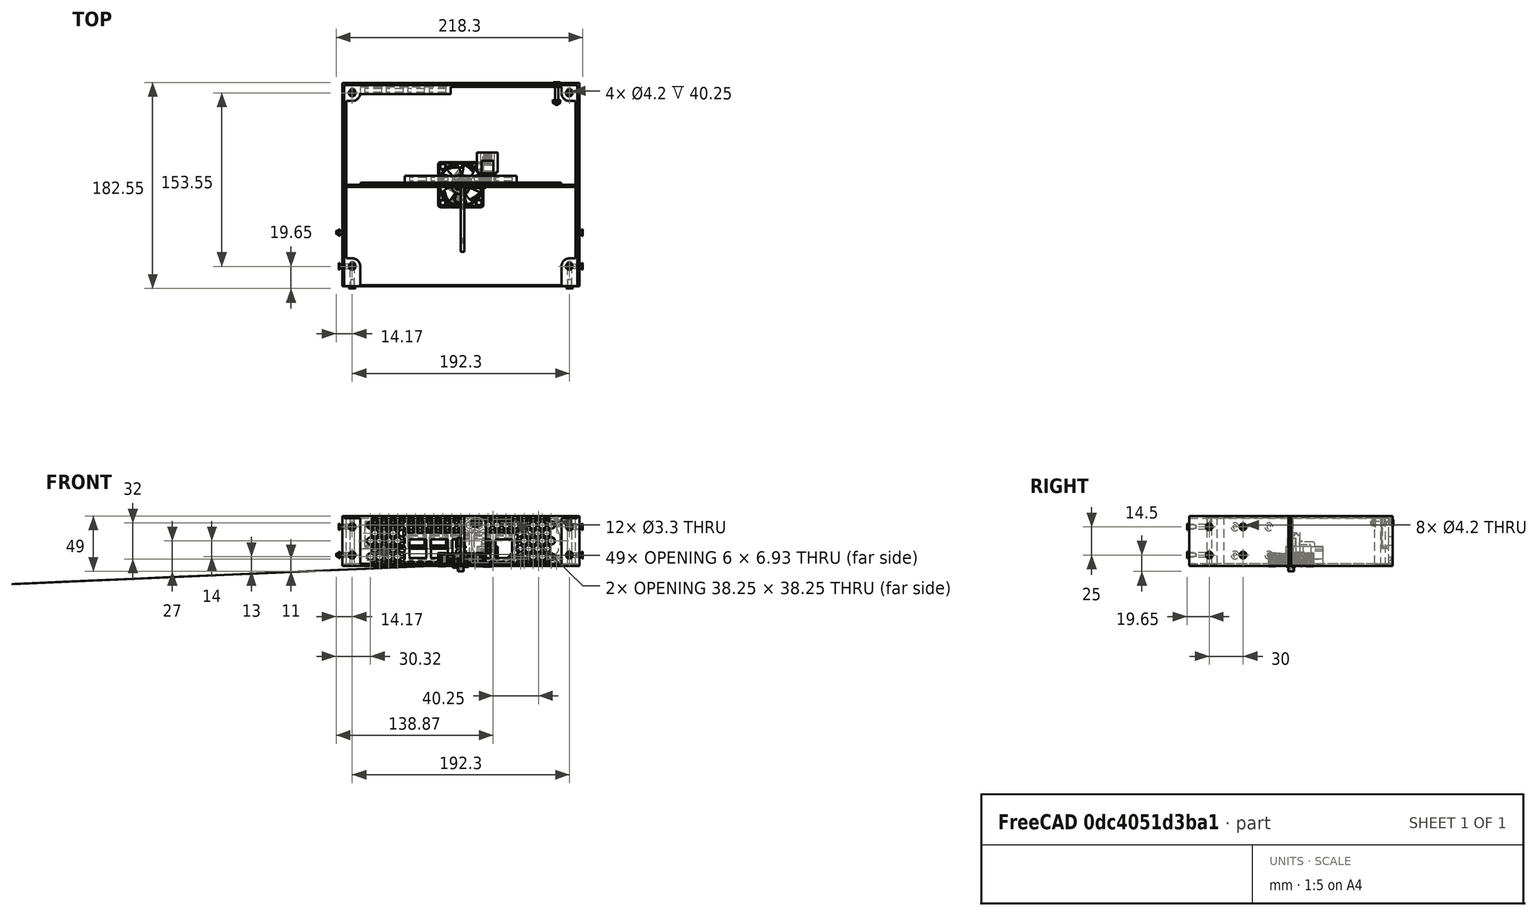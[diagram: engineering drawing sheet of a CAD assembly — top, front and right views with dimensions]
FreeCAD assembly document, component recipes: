
FREECAD ASSEMBLY — COMPONENT RECIPES ("Rack box")

This assembly document has 6 components, labeled P0..P5 below (a component is one placed body or linked part). 5 of them carry a construction recipe — the FreeCAD feature program that regenerates the part from scratch, quoted from this document or its linked companion documents; the rest are supplied as boundary geometry only. No exploded tour is included for this assembly.
COMPONENT P0 — recipe-attached ("Box001", modeled in this document).
Construction recipe (the document's own serialized feature program — sketch geometry with constraints, then the solid features built on it; lengths are millimeters unless a unit is written):

FEATURE [Sketcher::SketchObject] Sketch
  ArcFitTolerance = 1e-06
  AttachmentSupport = -> [XY_Plane002]
  ExternalTypes = [0]
  FullyConstrained = true
  MakeInternals = false
  MapMode = 2
  expr: Constraints[10] = <<Params>>.boxWidth
  expr: Constraints[11] = <<Params>>.boxLength
  sketch-geometry (5):
    g0: LineSegment StartX=-105 StartY=90 StartZ=0 EndX=-105 EndY=-90 EndZ=0
    g1: LineSegment StartX=-105 StartY=-90 StartZ=0 EndX=105 EndY=-90 EndZ=0
    g2: LineSegment StartX=105 StartY=-90 StartZ=0 EndX=105 EndY=90 EndZ=0
    g3: LineSegment StartX=105 StartY=90 StartZ=0 EndX=-105 EndY=90 EndZ=0
    g4: GeomPoint [constr] X=2e-16 Y=-2e-16 Z=0
  constraints (12):
    c: Coincident(g0,g1)
    c: Coincident(g1,g2)
    c: Coincident(g2,g3)
    c: Coincident(g3,g0)
    c: Vertical(g0)
    c: Vertical(g2)
    c: Horizontal(g1)
    c: Horizontal(g3)
    c: Symmetric(g2,g0,g4)
    c: Coincident(g4,g-1)
    c: DistanceX(g3,g3) = 210
    c: DistanceY(g2,g2) = 180
FEATURE [PartDesign::Pad] Pad  label="PROBLEMATIC_PAD"
  Direction = (0,0,1)
  Length = 44
  Length2 = 10
  Profile = -> Sketch
  ReferenceAxis = -> Sketch [N_Axis]
  Refine = true
  SideType = 0
  Suppressed = false
  Type = 0
  Type2 = 0
  expr: Length = <<Params>>.boxHeight * <<Params>>.rackUnit - <<Params>>.rackUnitTolerance
FEATURE [Sketcher::SketchObject] Sketch001
  ArcFitTolerance = 1e-06
  AttachmentSupport = -> [Pad]
  ExternalTypes = [0]
  FullyConstrained = true
  MakeInternals = false
  MapMode = 5
  Placement = pos=(0,0,44) rot=(0,0,1;0rad)
  expr: Constraints[10] = <<Params>>.boxWidth - 2 * <<Params>>.wallThickness
  expr: Constraints[11] = <<Params>>.boxLength - <<Params>>.wallThickness
  expr: Constraints[12] = <<Params>>.boxLength / 2 - <<Params>>.wallThickness
  sketch-geometry (5):
    g0: LineSegment StartX=-103.25 StartY=-90 StartZ=0 EndX=103.25 EndY=-90 EndZ=0
    g1: LineSegment StartX=103.25 StartY=-90 StartZ=0 EndX=103.25 EndY=88.25 EndZ=0
    g2: LineSegment StartX=103.25 StartY=88.25 StartZ=0 EndX=-103.25 EndY=88.25 EndZ=0
    g3: LineSegment StartX=-103.25 StartY=88.25 StartZ=0 EndX=-103.25 EndY=-90 EndZ=0
    g4: GeomPoint X=0 Y=-90 Z=0
  constraints (13):
    c: Coincident(g0,g1)
    c: Coincident(g1,g2)
    c: Coincident(g2,g3)
    c: Coincident(g3,g0)
    c: Horizontal(g0)
    c: Horizontal(g2)
    c: Vertical(g1)
    c: Vertical(g3)
    c: Symmetric(g0,g0,g4)
    c: PointOnObject(g4,g-2)
    c: DistanceX(g2,g2) = 206.5
    c: DistanceY(g3,g3) = 178.25
    c: DistanceY(g-1,g2) = 88.25
FEATURE [PartDesign::Pocket] Pocket
  BaseFeature = -> Pad
  Direction = (0,0,-1)
  Length = 0
  Length2 = 5
  Offset = -1.75
  Profile = -> Sketch001
  ReferenceAxis = -> Sketch001 [N_Axis]
  Refine = true
  SideType = 0
  Suppressed = false
  Type = 3
  Type2 = 0
  UpToFace = -> Pad [Face5]
  expr: Offset = -<<Params>>.wallThickness
FEATURE [Sketcher::SketchObject] Sketch002
  ArcFitTolerance = 1e-06
  AttachmentSupport = -> [Pocket]
  ExternalTypes = [0]
  FullyConstrained = true
  MakeInternals = false
  MapMode = 5
  Placement = pos=(0,0,1.75) rot=(0,0,1;0rad)
  expr: Constraints[0] = <<Params>>.M3InsertDiam
  expr: Constraints[23] = <<Params>>.boxWidth / 2 - <<Params>>.wallThickness
  expr: Constraints[25] = 17.6 mm
  expr: Constraints[26] = <<Params>>.boxLength / 2
  expr: Constraints[31] = <<Params>>.boxLength - <<Params>>.wallThickness
  expr: Constraints[36] = <<Params>>.wallThickness
  expr: Constraints[65] = <<Params>>.wallThickness
  sketch-geometry (27):
    g0: Circle CenterX=-96.15 CenterY=81.15 CenterZ=0 NormalX=0 NormalY=0 NormalZ=1 AngleXU=0 Radius=2.1
    g1: LineSegment StartX=-89.05 StartY=-90 StartZ=0 EndX=-89.05 EndY=-72.4 EndZ=0
    g2: Circle CenterX=-96.15 CenterY=-72.4 CenterZ=0 NormalX=0 NormalY=0 NormalZ=1 AngleXU=0 Radius=2.1
    g3: ArcOfCircle CenterX=-96.15 CenterY=81.15 CenterZ=0 NormalX=0 NormalY=0 NormalZ=1 AngleXU=0 Radius=7.1 StartAngle=4.71239 EndAngle=6.28319
    g4: ArcOfCircle CenterX=-96.15 CenterY=-72.4 CenterZ=0 NormalX=0 NormalY=0 NormalZ=1 AngleXU=0 Radius=7.1 StartAngle=2e-16 EndAngle=1.5708
    g5: LineSegment [constr] StartX=-96.15 StartY=81.15 StartZ=0 EndX=-96.15 EndY=-72.4 EndZ=0
    g6: LineSegment StartX=-89.05 StartY=-90 StartZ=0 EndX=-103.25 EndY=-90 EndZ=0
    g7: LineSegment StartX=-101.5 StartY=74.05 StartZ=0 EndX=-101.5 EndY=-65.3 EndZ=0
    g8: LineSegment StartX=-96.15 StartY=74.05 StartZ=0 EndX=-101.5 EndY=74.05 EndZ=0
    g9: LineSegment StartX=-101.5 StartY=-65.3 StartZ=0 EndX=-96.15 EndY=-65.3 EndZ=0
    g10: LineSegment StartX=-103.25 StartY=-90 StartZ=0 EndX=-103.25 EndY=88.25 EndZ=0
    g11: LineSegment StartX=-89.05 StartY=86.5 StartZ=0 EndX=0 EndY=86.5 EndZ=0
    g12: LineSegment StartX=-89.05 StartY=81.15 StartZ=0 EndX=-89.05 EndY=86.5 EndZ=0
    g13: LineSegment StartX=-103.25 StartY=88.25 StartZ=0 EndX=0 EndY=88.25 EndZ=0
    g14: LineSegment StartX=103.25 StartY=88.25 StartZ=0 EndX=0 EndY=88.25 EndZ=0
    g15: LineSegment StartX=89.05 StartY=86.5 StartZ=0 EndX=0 EndY=86.5 EndZ=0
    g16: LineSegment StartX=89.05 StartY=81.15 StartZ=0 EndX=89.05 EndY=86.5 EndZ=0
    g17: ArcOfCircle CenterX=96.15 CenterY=81.15 CenterZ=0 NormalX=0 NormalY=0 NormalZ=1 AngleXU=0 Radius=7.1 StartAngle=3.14159 EndAngle=4.71239
    g18: LineSegment StartX=96.15 StartY=74.05 StartZ=0 EndX=101.5 EndY=74.05 EndZ=0
    g19: LineSegment StartX=103.25 StartY=-90 StartZ=0 EndX=103.25 EndY=88.25 EndZ=0
    g20: Circle CenterX=96.15 CenterY=81.15 CenterZ=0 NormalX=0 NormalY=0 NormalZ=1 AngleXU=0 Radius=2.1
    g21: ArcOfCircle CenterX=96.15 CenterY=-72.4 CenterZ=0 NormalX=0 NormalY=0 NormalZ=1 AngleXU=0 Radius=7.1 StartAngle=1.5708 EndAngle=3.14159
    g22: LineSegment StartX=89.05 StartY=-90 StartZ=0 EndX=89.05 EndY=-72.4 EndZ=0
    g23: LineSegment StartX=89.05 StartY=-90 StartZ=0 EndX=103.25 EndY=-90 EndZ=0
    g24: LineSegment StartX=101.5 StartY=-65.3 StartZ=0 EndX=96.15 EndY=-65.3 EndZ=0
    g25: LineSegment StartX=101.5 StartY=74.05 StartZ=0 EndX=101.5 EndY=-65.3 EndZ=0
    g26: Circle CenterX=96.15 CenterY=-72.4 CenterZ=0 NormalX=0 NormalY=0 NormalZ=1 AngleXU=0 Radius=2.1
  constraints (66):
    c: Diameter(g0) = 4.2
    c: Vertical(g1)
    c: Equal(g0,g2)
    c: Coincident(g3,g0)
    c: Coincident(g4,g2)
    c: Tangent(g4,g1) = -1.5708
    c: Coincident(g5,g0)
    c: Coincident(g5,g2)
    c: Vertical(g5)
    c: Distance(g2,g1) = 5
    c: Coincident(g6,g1)
    c: Vertical(g7)
    c: Coincident(g8,g7)
    c: Horizontal(g8)
    c: Tangent(g8,g3) = 1.5708
    c: Coincident(g9,g7)
    c: Horizontal(g9)
    c: Tangent(g9,g4) = 1.5708
    c: Coincident(g10,g6)
    c: Distance(g0,g10) = 5
    c: Distance(g3,g0) = 5
    c: Horizontal(g11)
    c: Coincident(g12,g11)
    c: DistanceX(g6,g-1) = 103.25
    c: Vertical(g10)
    c: DistanceY(g6,g2) = 17.6
    c: DistanceY(g6,g-1) = 90
    c: Horizontal(g6)
    c: PointOnObject(g11,g-2)
    c: Tangent(g12,g3) = -1.5708
    c: Vertical(g12)
    c: DistanceY(g10,g10) = 178.25
    c: Equal(g8,g12)
    c: Coincident(g13,g10)
    c: PointOnObject(g13,g-2)
    c: Horizontal(g13)
    c: Distance(g11,g13) = 1.75
    c: Equal(g0,g20)
    c: Symmetric(g0,g20,g-2)
    c: Symmetric(g1,g22,g-2)
    c: Symmetric(g1,g22,g-2)
    c: Equal(g3,g17)
    c: Symmetric(g3,g17,g-2)
    c: Symmetric(g3,g17,g-2)
    c: Equal(g4,g21)
    c: Symmetric(g4,g21,g-2)
    c: Symmetric(g4,g21,g-2)
    c: Symmetric(g6,g23,g-2)
    c: Symmetric(g6,g23,g-2)
    c: Symmetric(g7,g25,g-2)
    c: Symmetric(g7,g25,g-2)
    c: Symmetric(g8,g18,g-2)
    c: Symmetric(g8,g18,g-2)
    c: Symmetric(g9,g24,g-2)
    c: Symmetric(g9,g24,g-2)
    c: Symmetric(g10,g19,g-2)
    c: Symmetric(g10,g19,g-2)
    c: Symmetric(g11,g15,g-2)
    c: Symmetric(g12,g16,g-2)
    c: Symmetric(g12,g16,g-2)
    c: Symmetric(g13,g14,g-2)
    c: Coincident(g15,g11)
    c: Coincident(g14,g13)
    c: Equal(g2,g26)
    c: Symmetric(g2,g26,g-2)
    c: DistanceX(g10,g7) = 1.75
FEATURE [PartDesign::Pad] Pad001
  BaseFeature = -> Pocket
  Direction = (0,0,1)
  Length = 10
  Length2 = 10
  Offset = 2
  Profile = -> Sketch002
  ReferenceAxis = -> Sketch002 [N_Axis]
  Refine = true
  SideType = 0
  Suppressed = false
  Type = 3
  Type2 = 0
  UpToFace = -> Pocket [Face5]
  expr: Offset = <<Params>>.wallThickness + <<Params>>.fitTol
FEATURE [Sketcher::SketchObject] Sketch003
  ArcFitTolerance = 1e-06
  AttachmentSupport = -> [Pad001]
  ExternalTypes = [0]
  FullyConstrained = true
  MakeInternals = false
  MapMode = 5
  Placement = pos=(0,-90,0) rot=(1,0,0;1.5708rad)
  expr: .Constraints.frontHole = <<Params>>.M3InsertDiam
  expr: Constraints[10] = <<Params>>.rackUnit * <<Params>>.boxHeight - <<Params>>.rackUnitTolerance
  expr: Constraints[11] = <<Params>>.boxWidth / 2 - (<<Params>>.wallThickness + 5 + <<Params>>.M3InsertDiam / 2)
  expr: Constraints[9] = <<Params>>.boxHeight * <<Params>>.rackUnit - <<Params>>.rackUnitTolerance - 2 * <<Params>>.frontHoleTopBottomSpace
  sketch-geometry (9):
    g0: LineSegment [constr] StartX=-96.15 StartY=44 StartZ=0 EndX=-96.15 EndY=0 EndZ=0
    g1: GeomPoint [constr] X=-96.15 Y=22 Z=0
    g2: Circle CenterX=-96.15 CenterY=34.5 CenterZ=0 NormalX=0 NormalY=0 NormalZ=1 AngleXU=0 Radius=2.1
    g3: Circle CenterX=-96.15 CenterY=9.5 CenterZ=0 NormalX=0 NormalY=0 NormalZ=1 AngleXU=0 Radius=2.1
    g4: Circle CenterX=96.15 CenterY=34.5 CenterZ=0 NormalX=0 NormalY=0 NormalZ=1 AngleXU=0 Radius=2.1
    g5: Circle CenterX=96.15 CenterY=9.5 CenterZ=0 NormalX=0 NormalY=0 NormalZ=1 AngleXU=0 Radius=2.1
    g6: LineSegment [constr] StartX=-96.15 StartY=0 StartZ=0 EndX=0 EndY=0 EndZ=0
    g7: LineSegment [constr] StartX=-96.15 StartY=34.5 StartZ=0 EndX=-96.15 EndY=9.5 EndZ=0
    g8: GeomPoint [constr] X=-96.15 Y=22 Z=0
  constraints (19):
    c: Vertical(g0)
    c: Symmetric(g0,g0,g1)
    c: PointOnObject(g2,g0)
    c: Diameter(g2) = 4.2  'frontHole'
    c: Equal(g3,g2)
    c: Equal(g2,g4)
    c: Symmetric(g2,g4,g-2)
    c: Equal(g3,g5)
    c: Symmetric(g3,g5,g-2)
    c: DistanceY(g3,g2) = 25
    c: DistanceY(g-1,g0) = 44
    c: DistanceX(g0,g-1) = 96.15
    c: Coincident(g6,g0)
    c: Coincident(g6,g-1)
    c: Horizontal(g6)
    c: Coincident(g7,g2)
    c: Coincident(g7,g3)
    c: Symmetric(g7,g7,g8)
    c: Coincident(g8,g1)
FEATURE [PartDesign::Pocket] Pocket001
  BaseFeature = -> Pad001
  Direction = (0,1,-2e-16)
  Length = 17.6
  Length2 = 5
  Offset = 2.1
  Profile = -> Sketch003
  ReferenceAxis = -> Sketch003 [N_Axis]
  Refine = true
  SideType = 0
  Suppressed = false
  Type = 0
  Type2 = 0
  UpToShape = -> [Pad001]
  expr: Length = 17.6
  expr: Offset = <<Params>>.M3InsertDiam / 2
FEATURE [Sketcher::SketchObject] Sketch010
  ArcFitTolerance = 1e-06
  AttachmentSupport = -> [Pocket001]
  ExternalTypes = [0]
  FullyConstrained = true
  MakeInternals = false
  MapMode = 5
  Placement = pos=(-105,0,0) rot=(0.57735,-0.57735,-0.57735;2.0944rad)
  expr: Constraints[15] = <<Params>>.M3InsertDiam
  expr: Constraints[17] = <<Params>>.rackUnit * <<Params>>.boxHeight - <<Params>>.rackUnitTolerance - 2 * <<Params>>.frontHoleTopBottomSpace
  expr: Constraints[20] = (<<Params>>.rackUnit * <<Params>>.boxHeight - <<Params>>.rackUnitTolerance) / 2
  expr: Constraints[21] = <<Params>>.boxLength / 2 - 17.6
  sketch-geometry (9):
    g0: LineSegment [constr] StartX=72.4 StartY=34.5 StartZ=0 EndX=42.4 EndY=34.5 EndZ=0
    g1: LineSegment [constr] StartX=42.4 StartY=34.5 StartZ=0 EndX=42.4 EndY=9.5 EndZ=0
    g2: LineSegment [constr] StartX=42.4 StartY=9.5 StartZ=0 EndX=72.4 EndY=9.5 EndZ=0
    g3: LineSegment [constr] StartX=72.4 StartY=9.5 StartZ=0 EndX=72.4 EndY=34.5 EndZ=0
    g4: Circle CenterX=42.4 CenterY=9.5 CenterZ=0 NormalX=0 NormalY=0 NormalZ=1 AngleXU=0 Radius=2.1
    g5: Circle CenterX=72.4 CenterY=9.5 CenterZ=0 NormalX=0 NormalY=0 NormalZ=1 AngleXU=0 Radius=2.1
    g6: Circle CenterX=42.4 CenterY=34.5 CenterZ=0 NormalX=0 NormalY=0 NormalZ=1 AngleXU=0 Radius=2.1
    g7: Circle CenterX=72.4 CenterY=34.5 CenterZ=0 NormalX=0 NormalY=0 NormalZ=1 AngleXU=0 Radius=2.1
    g8: GeomPoint [constr] X=72.4 Y=22 Z=0
  constraints (22):
    c: Coincident(g0,g1)
    c: Coincident(g1,g2)
    c: Coincident(g2,g3)
    c: Coincident(g3,g0)
    c: Horizontal(g0)
    c: Horizontal(g2)
    c: Vertical(g1)
    c: Vertical(g3)
    c: PointOnObject(g5,g2)
    c: DistanceX(g2,g2) = 30
    c: Coincident(g4,g1)
    c: Coincident(g6,g0)
    c: Equal(g7,g6)
    c: Equal(g6,g4)
    c: Equal(g4,g5)
    c: Diameter(g4) = 4.2
    c: Coincident(g0,g7)
    c: DistanceY(g1,g1) = 25
    c: PointOnObject(g5,g3)
    c: Symmetric(g3,g3,g8)
    c: DistanceY(g-1,g8) = 22
    c: DistanceX(g-1,g5) = 72.4
FEATURE [PartDesign::Pocket] Pocket004
  BaseFeature = -> Pocket001
  Direction = (1,0,0)
  Length = 0
  Length2 = 5
  Offset = 7.1
  Profile = -> Sketch010
  ReferenceAxis = -> Sketch010 [N_Axis]
  Refine = true
  SideType = 0
  Suppressed = false
  Type = 3
  Type2 = 0
  UpToFace = -> Pocket001 [Face3]
  expr: Offset = <<Params>>.M3InsertDiam / 2 + 5
FEATURE [PartDesign::Mirrored] Mirrored002
  BaseFeature = -> Pocket004
  MirrorPlane = -> YZ_Plane002
  Originals = -> [Pocket004]
  Refine = true
  Suppressed = false
  TransformMode = 0
FEATURE [Sketcher::SketchObject] Sketch014
  ArcFitTolerance = 1e-06
  AttachmentSupport = -> [Pocket001]
  ExternalTypes = [0]
  FullyConstrained = true
  MakeInternals = false
  MapMode = 5
  Placement = pos=(0,86.5,0) rot=(1,0,0;1.5708rad)
  expr: Constraints[19] = <<Params>>.M3ScrewHole
  expr: Constraints[20] = 39 / 2
  expr: Constraints[56] = (<<Params>>.rackUnit * <<Params>>.boxHeight - <<Params>>.rackUnitTolerance) / 2 - 32 / 2 - (min(<<Params>>.boxHeight; <<Params>>.fanAmountY) - 1) * (40 + <<Params>>.fitTol) / 2
  expr: Constraints[57] = <<Params>>.boxWidth / 2 - (<<Params>>.wallThickness + 5 + <<Params>>.M3InsertDiam + 5) - <<Params>>.fitTol
  sketch-geometry (22):
    g0: LineSegment [constr] StartX=52.8 StartY=6 StartZ=0 EndX=84.8 EndY=6 EndZ=0
    g1: LineSegment [constr] StartX=84.8 StartY=6 StartZ=0 EndX=84.8 EndY=38 EndZ=0
    g2: LineSegment [constr] StartX=84.8 StartY=38 StartZ=0 EndX=52.8 EndY=38 EndZ=0
    g3: LineSegment [constr] StartX=52.8 StartY=38 StartZ=0 EndX=52.8 EndY=6 EndZ=0
    g4: Circle CenterX=52.8 CenterY=38 CenterZ=0 NormalX=0 NormalY=0 NormalZ=1 AngleXU=0 Radius=1.65
    g5: Circle CenterX=84.8 CenterY=38 CenterZ=0 NormalX=0 NormalY=0 NormalZ=1 AngleXU=0 Radius=1.65
    g6: Circle CenterX=52.8 CenterY=6 CenterZ=0 NormalX=0 NormalY=0 NormalZ=1 AngleXU=0 Radius=1.65
    g7: Circle CenterX=84.8 CenterY=6 CenterZ=0 NormalX=0 NormalY=0 NormalZ=1 AngleXU=0 Radius=1.65
    g8: LineSegment [constr] StartX=84.8 StartY=6 StartZ=0 EndX=52.8 EndY=38 EndZ=0
    g9: ArcOfCircle CenterX=68.8 CenterY=22 CenterZ=0 NormalX=0 NormalY=0 NormalZ=1 AngleXU=0 Radius=19.5 StartAngle=0.196432 EndAngle=1.37436
    g10: ArcOfCircle CenterX=68.8 CenterY=22 CenterZ=0 NormalX=0 NormalY=0 NormalZ=1 AngleXU=0 Radius=19.5 StartAngle=1.76723 EndAngle=2.94516
    g11: ArcOfCircle CenterX=68.8 CenterY=22 CenterZ=0 NormalX=0 NormalY=0 NormalZ=1 AngleXU=0 Radius=19.5 StartAngle=3.33802 EndAngle=4.51596
    g12: ArcOfCircle CenterX=68.8 CenterY=22 CenterZ=0 NormalX=0 NormalY=0 NormalZ=1 AngleXU=0 Radius=19.5 StartAngle=4.90882 EndAngle=6.08675
    g13: LineSegment StartX=49.675 StartY=25.8058 StartZ=0 EndX=49.675 EndY=18.1942 EndZ=0
    g14: LineSegment StartX=64.9942 StartY=2.875 StartZ=0 EndX=72.6058 EndY=2.875 EndZ=0
    g15: LineSegment StartX=87.925 StartY=18.1942 StartZ=0 EndX=87.925 EndY=25.8058 EndZ=0
    g16: LineSegment StartX=72.6058 StartY=41.125 StartZ=0 EndX=64.9942 EndY=41.125 EndZ=0
    g17: LineSegment [constr] StartX=48.8 StartY=2 StartZ=0 EndX=88.8 EndY=2 EndZ=0
    g18: LineSegment [constr] StartX=88.8 StartY=2 StartZ=0 EndX=88.8 EndY=42 EndZ=0
    g19: LineSegment [constr] StartX=88.8 StartY=42 StartZ=0 EndX=48.8 EndY=42 EndZ=0
    g20: LineSegment [constr] StartX=48.8 StartY=42 StartZ=0 EndX=48.8 EndY=2 EndZ=0
    g21: GeomPoint [constr] X=68.8 Y=22 Z=0
  constraints (58):
    c: Coincident(g0,g1)
    c: Coincident(g1,g2)
    c: Coincident(g2,g3)
    c: Coincident(g3,g0)
    c: Horizontal(g0)
    c: Horizontal(g2)
    c: Vertical(g1)
    c: Vertical(g3)
    c: Equal(g2,g3)
    c: DistanceX(g2,g2) = 32
    c: Coincident(g4,g2)
    c: Coincident(g5,g1)
    c: Coincident(g6,g0)
    c: Coincident(g7,g0)
    c: Coincident(g8,g0)
    c: Coincident(g8,g2)
    c: Equal(g4,g5)
    c: Equal(g5,g7)
    c: Equal(g7,g6)
    c: Diameter(g4) = 3.3
    c: Radius(g9) = 19.5
    c: Symmetric(g8,g8,g9)
    c: Coincident(g10,g9)
    c: Coincident(g11,g9)
    c: Coincident(g12,g9)
    c: Equal(g12,g10)
    c: Equal(g10,g11)
    c: Equal(g11,g9)
    c: Coincident(g13,g10)
    c: Coincident(g13,g11)
    c: Coincident(g14,g11)
    c: Coincident(g14,g12)
    c: Coincident(g15,g12)
    c: Coincident(g15,g9)
    c: Coincident(g16,g9)
    c: Coincident(g16,g10)
    c: Equal(g16,g14)
    c: Equal(g14,g13)
    c: Equal(g13,g15)
    c: Horizontal(g16)
    c: Horizontal(g14)
    c: Vertical(g13)
    c: Vertical(g15)
    c: Coincident(g17,g18)
    c: Coincident(g18,g19)
    c: Coincident(g19,g20)
    c: Coincident(g20,g17)
    c: Horizontal(g17)
    c: Horizontal(g19)
    c: Vertical(g18)
    c: Vertical(g20)
    c: Symmetric(g19,g17,g21)
    c: Distance(g18,g20) = 40
    c: Distance(g17,g19) = 40
    c: Symmetric(g8,g8,g21)
    c: Distance(g19,g16) = 0.875
    c: DistanceY(g-1,g0) = 6
    c: DistanceX(g-1,g17) = 88.8
FEATURE [PartDesign::Pocket] Pocket006  label="fanHole"
  BaseFeature = -> Mirrored002
  Direction = (0,1,-2e-16)
  Length = 5
  Length2 = 5
  Profile = -> Sketch014
  ReferenceAxis = -> Sketch014 [N_Axis]
  Refine = true
  SideType = 0
  Suppressed = false
  Type = 1
  Type2 = 0
FEATURE [PartDesign::LinearPattern] LinearPattern003
  Direction = -> Sketch014 [H_Axis]
  Length = 40.25
  Length2 = 100
  Mode = 1
  Mode2 = 0
  Occurrences = 2
  Occurrences2 = 1
  Offset = 40.25
  Offset2 = 10
  Refine = true
  Reversed = true
  Reversed2 = false
  SpacingPattern = [0]
  SpacingPattern2 = [0]
  Spacings = [-1]
  Suppressed = false
  TransformMode = 0
  expr: Occurrences = min(3; <<Params>>.fanAmountX)
  expr: Offset = 40 + <<Params>>.fitTol
FEATURE [PartDesign::LinearPattern] LinearPattern004
  Direction = -> Sketch014 [V_Axis]
  Length = 40.25
  Length2 = 100
  Mode = 1
  Mode2 = 0
  Occurrences = 1
  Occurrences2 = 1
  Offset = 40.25
  Offset2 = 10
  Refine = true
  Reversed2 = false
  SpacingPattern = [0]
  SpacingPattern2 = [0]
  Spacings2 = [0]
  Suppressed = false
  TransformMode = 0
  expr: Occurrences = min(<<Params>>.boxHeight; <<Params>>.fanAmountY)
  expr: Offset = 40 + <<Params>>.fitTol
FEATURE [Sketcher::SketchObject] Sketch030  label="KeystoneSlab"
  ArcFitTolerance = 1e-06
  AttachmentSupport = -> [Mirrored002]
  ExternalTypes = [0]
  FullyConstrained = true
  MakeInternals = false
  MapMode = 5
  Placement = pos=(0,90,0) rot=(0,0.707107,0.707107;3.14159rad)
  expr: Constraints[10] = 4.2 + (<<Params>>.keystoneHoleWidth + 4.2) * <<Params>>.keystoneBackX
  expr: Constraints[11] = <<Params>>.rackUnit - <<Params>>.rackUnitTolerance - <<Params>>.wallThickness - <<Params>>.fitTol
  expr: Constraints[8] = <<Params>>.boxWidth / 2 - (<<Params>>.wallThickness + 5 + <<Params>>.M3InsertDiam + 5)
  expr: Constraints[9] = 3 + <<Params>>.keystoneCatchHeight + 4
  sketch-geometry (4):
    g0: LineSegment StartX=89.05 StartY=42 StartZ=0 EndX=8.85 EndY=42 EndZ=0
    g1: LineSegment StartX=8.85 StartY=42 StartZ=0 EndX=8.85 EndY=15.2 EndZ=0
    g2: LineSegment StartX=8.85 StartY=15.2 StartZ=0 EndX=89.05 EndY=15.2 EndZ=0
    g3: LineSegment StartX=89.05 StartY=15.2 StartZ=0 EndX=89.05 EndY=42 EndZ=0
  constraints (12):
    c: Coincident(g0,g1)
    c: Coincident(g1,g2)
    c: Coincident(g2,g3)
    c: Coincident(g3,g0)
    c: Horizontal(g0)
    c: Horizontal(g2)
    c: Vertical(g1)
    c: Vertical(g3)
    c: DistanceX(g-1,g2) = 89.05
    c: DistanceY(g3,g3) = 26.8
    c: DistanceX(g2,g2) = 80.2
    c: DistanceY(g-1,g0) = 42
FEATURE [Sketcher::SketchObject] Sketch032  label="KeystoneHoleSketch"
  ArcFitTolerance = 1e-06
  AttachmentSupport = -> [Pad]
  ExternalTypes = [0]
  FullyConstrained = true
  MakeInternals = false
  MapMode = 5
  Placement = pos=(0,90,0) rot=(0,0.707107,0.707107;3.14159rad)
  expr: Constraints[10] = <<Params>>.boxWidth / 2 - (<<Params>>.wallThickness + 5 + <<Params>>.M3InsertDiam + 5) - 4.2
  expr: Constraints[11] = <<Params>>.rackUnit - <<Params>>.rackUnitTolerance - <<Params>>.wallThickness - <<Params>>.keystoneCatchHeight - 4.2 - <<Params>>.fitTol
  expr: Constraints[8] = <<Params>>.keystoneHoleWidth
  expr: Constraints[9] = <<Params>>.keystoneHoleHeight
  sketch-geometry (4):
    g0: LineSegment StartX=70.05 StartY=34.8 StartZ=0 EndX=70.05 EndY=18 EndZ=0
    g1: LineSegment StartX=70.05 StartY=18 StartZ=0 EndX=84.85 EndY=18 EndZ=0
    g2: LineSegment StartX=84.85 StartY=18 StartZ=0 EndX=84.85 EndY=34.8 EndZ=0
    g3: LineSegment StartX=84.85 StartY=34.8 StartZ=0 EndX=70.05 EndY=34.8 EndZ=0
  constraints (12):
    c: Coincident(g0,g1)
    c: Coincident(g1,g2)
    c: Coincident(g2,g3)
    c: Coincident(g3,g0)
    c: Vertical(g0)
    c: Vertical(g2)
    c: Horizontal(g1)
    c: Horizontal(g3)
    c: DistanceX(g3,g3) = 14.8
    c: DistanceY(g2,g2) = 16.8
    c: DistanceX(g-1,g1) = 84.85
    c: DistanceY(g-1,g1) = 18
FEATURE [Sketcher::SketchObject] Sketch034  label="CatchHolesSketchBack"
  ArcFitTolerance = 1e-06
  AttachmentSupport = -> [Mirrored002]
  ExternalTypes = [0]
  FullyConstrained = true
  MakeInternals = false
  MapMode = 5
  Placement = pos=(-89.05,0,0) rot=(0.57735,0.57735,0.57735;2.0944rad)
  expr: Constraints[21] = <<Params>>.keystoneCatchHeight
  expr: Constraints[22] = <<Params>>.rackUnit - <<Params>>.rackUnitTolerance - <<Params>>.wallThickness - <<Params>>.keystoneCatchHeight - 4.2 - <<Params>>.fitTol
  expr: Constraints[23] = <<Params>>.boxLength / 2 - <<Params>>.keystoneCatchDepth
  sketch-geometry (8):
    g0: LineSegment StartX=81.8 StartY=18 StartZ=0 EndX=81.8 EndY=16.5 EndZ=0
    g1: LineSegment StartX=81.8 StartY=16.5 StartZ=0 EndX=84.8 EndY=16.5 EndZ=0
    g2: LineSegment StartX=84.8 StartY=16.5 StartZ=0 EndX=84.8 EndY=18 EndZ=0
    g3: LineSegment StartX=84.8 StartY=18 StartZ=0 EndX=81.8 EndY=18 EndZ=0
    g4: LineSegment StartX=87.8 StartY=39.3 StartZ=0 EndX=87.8 EndY=37.8 EndZ=0
    g5: LineSegment StartX=87.8 StartY=37.8 StartZ=0 EndX=84.8 EndY=37.8 EndZ=0
    g6: LineSegment StartX=84.8 StartY=37.8 StartZ=0 EndX=84.8 EndY=39.3 EndZ=0
    g7: LineSegment StartX=84.8 StartY=39.3 StartZ=0 EndX=87.8 EndY=39.3 EndZ=0
  constraints (24):
    c: Coincident(g0,g1)
    c: Coincident(g1,g2)
    c: Coincident(g2,g3)
    c: Coincident(g3,g0)
    c: Vertical(g0)
    c: Vertical(g2)
    c: Horizontal(g1)
    c: Horizontal(g3)
    c: DistanceX(g3,g3) = 3
    c: DistanceY(g2,g2) = 1.5
    c: Coincident(g4,g5)
    c: Coincident(g5,g6)
    c: Coincident(g6,g7)
    c: Coincident(g7,g4)
    c: Vertical(g4)
    c: Vertical(g6)
    c: Horizontal(g5)
    c: Horizontal(g7)
    c: Equal(g5,g3)
    c: Equal(g6,g2)
    c: PointOnObject(g2,g6)
    c: DistanceY(g2,g5) = 19.8
    c: DistanceY(g-1,g2) = 18
    c: DistanceX(g-1,g0) = 81.8
FEATURE [PartDesign::LinearPattern] LinearPattern
  Direction = -> Sketch032 [H_Axis]
  Length = 57
  Length2 = 100
  Mode = 1
  Mode2 = 0
  Occurrences = 4
  Occurrences2 = 1
  Offset = 19
  Offset2 = 10
  Refine = true
  Reversed = true
  Reversed2 = false
  SpacingPattern = [0]
  SpacingPattern2 = [0]
  Spacings = [-1,-1,-1]
  Suppressed = false
  TransformMode = 0
  expr: Occurrences = <<Params>>.keystoneBackX
  expr: Offset = <<Params>>.keystoneHoleWidth + 4.2
FEATURE [PartDesign::Chamfer] Chamfer007
  Angle = 45
  Base = -> Pocket006 [Edge132,Edge152,Edge154,Edge134]
  BaseFeature = -> Pocket006
  ChamferType = 0
  FlipDirection = false
  Refine = true
  Size = 1.4
  Size2 = 1
  SupportTransform = false
  Suppressed = false
  UseAllEdges = false
FEATURE [PartDesign::MultiTransform] MultiTransform001
  BaseFeature = -> Chamfer007
  Originals = -> [Pocket006,Chamfer007]
  Refine = true
  Suppressed = false
  TransformMode = 0
  Transformations = -> [LinearPattern003,LinearPattern004]
FEATURE [PartDesign::Pad] Pad012  label="KeystoneSlabPad"
  BaseFeature = -> MultiTransform001
  Direction = (0,1,-2e-16)
  Length = 9.75
  Length2 = 10
  Profile = -> Sketch030
  ReferenceAxis = -> Sketch030 [N_Axis]
  Refine = true
  Reversed = true
  SideType = 0
  Suppressed = false
  Type = 0
  Type2 = 0
  expr: Length = <<Params>>.keystoneStopDepth
FEATURE [PartDesign::Pocket] Pocket011  label="KeystoneHolePocket001"
  BaseFeature = -> Pad012
  Direction = (0,-1,2e-16)
  Length = 5
  Length2 = 5
  Profile = -> Sketch032
  ReferenceAxis = -> Sketch032 [N_Axis]
  Refine = true
  SideType = 0
  Suppressed = false
  Type = 1
  Type2 = 0
FEATURE [Sketcher::SketchObject] Sketch033  label="KeystoneCatchSketch"
  ArcFitTolerance = 1e-06
  AttachmentSupport = -> [Pocket011]
  ExternalTypes = [0]
  FullyConstrained = true
  MakeInternals = false
  MapMode = 5
  Placement = pos=(0,80.25,-4.25e-14) rot=(1,0,0;1.5708rad)
  expr: Constraints[10] = <<Params>>.boxWidth / 2 - (<<Params>>.wallThickness + 5 + <<Params>>.M3InsertDiam + 5) - 4.2
  expr: Constraints[11] = <<Params>>.rackUnit - <<Params>>.rackUnitTolerance - <<Params>>.wallThickness - <<Params>>.keystoneCatchHeight - 4.2 - <<Params>>.fitTol
  expr: Constraints[8] = <<Params>>.keystoneCatchHeight
  expr: Constraints[9] = <<Params>>.keystoneHoleWidth
  sketch-geometry (4):
    g0: LineSegment StartX=-84.85 StartY=37.8 StartZ=0 EndX=-84.85 EndY=18 EndZ=0
    g1: LineSegment StartX=-84.85 StartY=18 StartZ=0 EndX=-70.05 EndY=18 EndZ=0
    g2: LineSegment StartX=-70.05 StartY=18 StartZ=0 EndX=-70.05 EndY=37.8 EndZ=0
    g3: LineSegment StartX=-70.05 StartY=37.8 StartZ=0 EndX=-84.85 EndY=37.8 EndZ=0
  constraints (12):
    c: Coincident(g0,g1)
    c: Coincident(g1,g2)
    c: Coincident(g2,g3)
    c: Coincident(g3,g0)
    c: Vertical(g0)
    c: Vertical(g2)
    c: Horizontal(g1)
    c: Horizontal(g3)
    c: DistanceY(g2,g2) = 19.8
    c: DistanceX(g3,g3) = 14.8
    c: DistanceX(g0,g-1) = 84.85
    c: DistanceY(g-1,g0) = 18
FEATURE [PartDesign::Pocket] Pocket012  label="KeystoneCatchPocket"
  BaseFeature = -> Pocket011
  Direction = (0,1,-2e-16)
  Length = 8.2
  Length2 = 5
  Profile = -> Sketch033
  ReferenceAxis = -> Sketch033 [N_Axis]
  Refine = true
  SideType = 0
  Suppressed = false
  Type = 0
  Type2 = 0
  expr: Length = <<Params>>.keystoneCatchDepth
FEATURE [PartDesign::Pocket] Pocket013  label="CatchHolesPocketBox"
  BaseFeature = -> Pocket012
  Direction = (-1,0,0)
  Length = 19
  Length2 = -4.2
  Profile = -> Sketch034
  ReferenceAxis = -> Sketch034 [N_Axis]
  Refine = true
  Reversed = true
  SideType = 1
  Suppressed = false
  Type = 0
  Type2 = 0
  expr: Length = <<Params>>.keystoneHoleWidth + 4.2
FEATURE [PartDesign::Chamfer] Chamfer006
  Angle = 45
  Base = -> Pocket013 [Edge99,Edge260,Edge97]
  BaseFeature = -> Pocket013
  ChamferType = 0
  FlipDirection = false
  Refine = true
  Size = 1
  Size2 = 1
  SupportTransform = false
  Suppressed = false
  UseAllEdges = false
FEATURE [PartDesign::MultiTransform] MultiTransform
  BaseFeature = -> Chamfer006
  Originals = -> [Pocket011,Pocket012,Pocket013,Chamfer006]
  Refine = true
  Suppressed = false
  TransformMode = 0
  Transformations = -> [LinearPattern]
FEATURE [PartDesign::Body] Body  label="box"
  AllowCompound = false
  Group = -> [Sketch,Pad,Sketch001,Pocket,Sketch002,Pad001,Sketch003,Pocket001,Sketch010,Pocket004,Mirrored002,Sketch014,Pocket006,Chamfer007,MultiTransform001,LinearPattern003,LinearPattern004,Sketch030,Pad012,Sketch032,Pocket011,Sketch033,Pocket012,Sketch034,Pocket013,Chamfer006,MultiTransform,LinearPattern]
  Origin = -> Origin002
  Tip = -> MultiTransform
COMPONENT P1 — recipe-attached ("Ear 3D001", modeled in this document).
Construction recipe (the document's own serialized feature program — sketch geometry with constraints, then the solid features built on it; lengths are millimeters unless a unit is written):

FEATURE [Sketcher::SketchObject] Sketch011
  ArcFitTolerance = 1e-06
  AttachmentSupport = -> [YZ_Plane013]
  ExternalTypes = [0]
  FullyConstrained = true
  MakeInternals = false
  MapMode = 5
  Placement = pos=(0,0,0) rot=(0.57735,0.57735,0.57735;2.0944rad)
  expr: Constraints[14] = <<Params>>.M3ScrewHole
  expr: Constraints[28] = <<Params>>.boxHeight * <<Params>>.rackUnit - <<Params>>.rackUnitTolerance - 2 * <<Params>>.frontHoleTopBottomSpace
  expr: Constraints[30] = <<Params>>.frontThickness + 17.6
  expr: Constraints[32] = (<<Params>>.rackUnit * <<Params>>.boxHeight - <<Params>>.rackUnitTolerance) / 2
  expr: Constraints[33] = <<Params>>.rackUnit * <<Params>>.boxHeight - <<Params>>.rackUnitTolerance
  sketch-geometry (14):
    g0: LineSegment StartX=0 StartY=44 StartZ=0 EndX=-59.6 EndY=44 EndZ=0
    g1: LineSegment StartX=-59.6 StartY=44 StartZ=0 EndX=-59.6 EndY=0 EndZ=0
    g2: LineSegment StartX=-59.6 StartY=0 StartZ=0 EndX=0 EndY=0 EndZ=0
    g3: LineSegment StartX=0 StartY=0 StartZ=0 EndX=0 EndY=44 EndZ=0
    g4: LineSegment [constr] StartX=-49.6 StartY=9.5 StartZ=0 EndX=-49.6 EndY=0 EndZ=0
    g5: Circle CenterX=-49.6 CenterY=34.5 CenterZ=0 NormalX=0 NormalY=0 NormalZ=1 AngleXU=0 Radius=1.65
    g6: Circle CenterX=-19.6 CenterY=34.5 CenterZ=0 NormalX=0 NormalY=0 NormalZ=1 AngleXU=0 Radius=1.65
    g7: Circle CenterX=-49.6 CenterY=9.5 CenterZ=0 NormalX=0 NormalY=0 NormalZ=1 AngleXU=0 Radius=1.65
    g8: Circle CenterX=-19.6 CenterY=9.5 CenterZ=0 NormalX=0 NormalY=0 NormalZ=1 AngleXU=0 Radius=1.65
    g9: LineSegment [constr] StartX=-49.6 StartY=34.5 StartZ=0 EndX=-19.6 EndY=34.5 EndZ=0
    g10: LineSegment [constr] StartX=-19.6 StartY=34.5 StartZ=0 EndX=-19.6 EndY=9.5 EndZ=0
    g11: LineSegment [constr] StartX=-19.6 StartY=9.5 StartZ=0 EndX=-49.6 EndY=9.5 EndZ=0
    g12: LineSegment [constr] StartX=-49.6 StartY=9.5 StartZ=0 EndX=-49.6 EndY=34.5 EndZ=0
    g13: GeomPoint [constr] X=-19.6 Y=22 Z=0
  constraints (36):
    c: Coincident(g0,g1)
    c: Coincident(g1,g2)
    c: Coincident(g2,g3)
    c: Coincident(g3,g0)
    c: Horizontal(g0)
    c: Horizontal(g2)
    c: Vertical(g1)
    c: Vertical(g3)
    c: PointOnObject(g4,g2)
    c: Vertical(g4)
    c: Coincident(g7,g4)
    c: Equal(g7,g5)
    c: Equal(g5,g6)
    c: Equal(g6,g8)
    c: Diameter(g7) = 3.3
    c: Coincident(g9,g5)
    c: Coincident(g9,g6)
    c: Horizontal(g9)
    c: Coincident(g10,g6)
    c: Coincident(g10,g8)
    c: Vertical(g10)
    c: Coincident(g11,g8)
    c: Coincident(g11,g4)
    c: Horizontal(g11)
    c: Coincident(g12,g4)
    c: Coincident(g12,g5)
    c: Vertical(g12)
    c: DistanceX(g9,g9) = 30
    c: DistanceY(g10,g10) = 25
    c: PointOnObject(g-1,g2)
    c: DistanceX(g8,g2) = 19.6
    c: Symmetric(g10,g10,g13)
    c: DistanceY(g-1,g13) = 22
    c: DistanceY(g3,g3) = 44
    c: PointOnObject(g-1,g3)
    c: DistanceX(g1,g8) = 40
FEATURE [PartDesign::Pad] Pad006
  Direction = (1,0,0)
  Length = 3
  Length2 = 10
  Placement = pos=(0,0,0) rot=(1,1,1;2.0944rad)
  Profile = -> Sketch011
  ReferenceAxis = -> Sketch011 [N_Axis]
  Refine = true
  SideType = 0
  Suppressed = false
  Type = 0
  Type2 = 0
  expr: Length = <<Params>>.rackEarThick3D
FEATURE [PartDesign::Chamfer] Chamfer003
  Angle = 45
  Base = -> Pad006 [Edge15,Edge18,Edge21,Edge24]
  BaseFeature = -> Pad006
  ChamferType = 0
  FlipDirection = false
  Placement = pos=(0,0,0) rot=(1,1,1;2.0944rad)
  Refine = true
  Size = 1.85
  Size2 = 1
  SupportTransform = false
  Suppressed = false
  UseAllEdges = false
  expr: Size = min(<<Params>>.iso10642coneDetph; <<Params>>.rackEarThick3D - 0.01)
FEATURE [Sketcher::SketchObject] Sketch012
  ArcFitTolerance = 1e-06
  AttachmentSupport = -> [Chamfer003]
  ExternalGeometry = -> [Chamfer003]
  ExternalTypes = [0]
  FullyConstrained = true
  MakeInternals = false
  MapMode = 5
  Placement = pos=(3,-7e-16,3e-16) rot=(0.57735,0.57735,0.57735;2.0944rad)
  expr: Constraints[10] = <<Params>>.rackEarThick3D
  sketch-geometry (4):
    g0: LineSegment StartX=3.6e-15 StartY=44 StartZ=0 EndX=-3 EndY=44 EndZ=0
    g1: LineSegment StartX=-3 StartY=44 StartZ=0 EndX=-3 EndY=0 EndZ=0
    g2: LineSegment StartX=-3 StartY=0 StartZ=0 EndX=3.6e-15 EndY=0 EndZ=0
    g3: LineSegment StartX=3.6e-15 StartY=0 StartZ=0 EndX=3.6e-15 EndY=44 EndZ=0
  constraints (11):
    c: Coincident(g0,g1)
    c: Coincident(g1,g2)
    c: Coincident(g2,g3)
    c: Coincident(g3,g0)
    c: Horizontal(g0)
    c: Horizontal(g2)
    c: Vertical(g1)
    c: Vertical(g3)
    c: Coincident(g0,g-3)
    c: PointOnObject(g-3,g2)
    c: DistanceX(g0,g0) = 3
FEATURE [PartDesign::Pad] Pad007
  BaseFeature = -> Chamfer003
  Direction = (1,0,0)
  Length = 19
  Length2 = 10
  Placement = pos=(0,0,0) rot=(1,1,1;2.0944rad)
  Profile = -> Sketch012
  ReferenceAxis = -> Sketch012 [N_Axis]
  Refine = true
  SideType = 0
  Suppressed = false
  Type = 0
  Type2 = 0
  expr: Length = (<<Params>>.rackTotalWidth - <<Params>>.boxWidth) / 2 - <<Params>>.rackEarThick3D
FEATURE [Sketcher::SketchObject] Sketch013
  ArcFitTolerance = 1e-06
  AttachmentSupport = -> [Pad007]
  ExternalTypes = [0]
  FullyConstrained = true
  MakeInternals = false
  MapMode = 5
  Placement = pos=(0,3e-16,0) rot=(0.57735,0.57735,0.57735;4.18879rad)
  expr: Constraints[0] = <<Params>>.rackHoleDiam
  expr: Constraints[18] = <<Params>>.rackHoleDiam / 2 + <<Params>>.fitTol
  expr: Constraints[1] = <<Params>>.boxHeight > 1 ? <<Params>>.rackUnit * <<Params>>.boxHeight - (<<Params>>.rackUnit - <<Params>>.rackUnitTolerance) : <<Params>>.rackHoleSpacing * 2
  expr: Constraints[6] = <<Params>>.boxHeight > 1 ? <<Params>>.rackUnit / 2 - <<Params>>.rackUnitTolerance / 2 : <<Params>>.rackUnit / 2 - <<Params>>.rackUnitTolerance / 2 - <<Params>>.rackHoleSpacing
  expr: Constraints[7] = (<<Params>>.rackHoleSpread - <<Params>>.boxWidth) / 2
  sketch-geometry (13):
    g0: Circle [constr] CenterX=37.875 CenterY=13.2625 CenterZ=0 NormalX=0 NormalY=0 NormalZ=1 AngleXU=0 Radius=3
    g1: LineSegment [constr] StartX=37.875 StartY=13.2625 StartZ=0 EndX=6.125 EndY=13.2625 EndZ=0
    g2: Circle [constr] CenterX=6.125 CenterY=13.2625 CenterZ=0 NormalX=0 NormalY=0 NormalZ=1 AngleXU=0 Radius=3
    g3: ArcOfCircle CenterX=6.125 CenterY=14.7625 CenterZ=0 NormalX=0 NormalY=0 NormalZ=1 AngleXU=0 Radius=3.25 StartAngle=2e-16 EndAngle=3.14159
    g4: ArcOfCircle CenterX=6.125 CenterY=11.7625 CenterZ=0 NormalX=0 NormalY=0 NormalZ=1 AngleXU=0 Radius=3.25 StartAngle=3.14159 EndAngle=6.28319
    g5: LineSegment StartX=9.375 StartY=14.7625 StartZ=0 EndX=9.375 EndY=11.7625 EndZ=0
    g6: LineSegment StartX=2.875 StartY=14.7625 StartZ=0 EndX=2.875 EndY=11.7625 EndZ=0
    g7: LineSegment [constr] StartX=6.125 StartY=14.7625 StartZ=0 EndX=6.125 EndY=11.7625 EndZ=0
    g8: ArcOfCircle CenterX=37.875 CenterY=14.7625 CenterZ=0 NormalX=0 NormalY=0 NormalZ=1 AngleXU=0 Radius=3.25 StartAngle=2e-16 EndAngle=3.14159
    g9: ArcOfCircle CenterX=37.875 CenterY=11.7625 CenterZ=0 NormalX=0 NormalY=0 NormalZ=1 AngleXU=0 Radius=3.25 StartAngle=3.14159 EndAngle=6.28319
    g10: LineSegment StartX=41.125 StartY=14.7625 StartZ=0 EndX=41.125 EndY=11.7625 EndZ=0
    g11: LineSegment StartX=34.625 StartY=14.7625 StartZ=0 EndX=34.625 EndY=11.7625 EndZ=0
    g12: LineSegment [constr] StartX=37.875 StartY=14.7625 StartZ=0 EndX=37.875 EndY=11.7625 EndZ=0
  constraints (30):
    c: Diameter(g0) = 6
    c: Distance(g1,g1) = 31.75
    c: Coincident(g2,g1)
    c: Equal(g2,g0)
    c: Coincident(g1,g0)
    c: Horizontal(g1)
    c: DistanceX(g-1,g1) = 6.125
    c: Distance(g1,g-1) = 13.2625
    c: Tangent(g3,g5) = 1.5708
    c: Tangent(g3,g6) = -1.5708
    c: Tangent(g4,g5) = 1.5708
    c: Tangent(g4,g6) = -1.5708
    c: Equal(g3,g4)
    c: Coincident(g7,g3)
    c: Coincident(g7,g4)
    c: Symmetric(g7,g7,g1)
    c: Vertical(g7)
    c: DistanceY(g4,g3) = 3
    c: Radius(g3) = 3.25
    c: Tangent(g8,g10) = 1.5708
    c: Tangent(g8,g11) = -1.5708
    c: Tangent(g9,g10) = 1.5708
    c: Tangent(g9,g11) = -1.5708
    c: Equal(g8,g9)
    c: Coincident(g12,g8)
    c: Coincident(g12,g9)
    c: Symmetric(g12,g12,g0)
    c: Vertical(g12)
    c: Equal(g8,g3)
    c: Equal(g5,g11)
FEATURE [PartDesign::Pocket] Pocket005
  BaseFeature = -> Pad007
  Direction = (0,-1,0)
  Length = 5
  Length2 = 5
  Placement = pos=(0,0,0) rot=(1,1,1;2.0944rad)
  Profile = -> Sketch013
  ReferenceAxis = -> Sketch013 [N_Axis]
  Refine = true
  SideType = 0
  Suppressed = false
  Type = 1
  Type2 = 0
FEATURE [PartDesign::Fillet] Fillet
  Base = -> Pocket005 [Edge13]
  BaseFeature = -> Pocket005
  Placement = pos=(0,0,0) rot=(1,1,1;2.0944rad)
  Radius = 1.5
  Refine = true
  SupportTransform = false
  Suppressed = false
  UseAllEdges = false
FEATURE [PartDesign::Fillet] Fillet001
  Base = -> Fillet [Edge21,Edge11]
  BaseFeature = -> Fillet
  Placement = pos=(0,0,0) rot=(1,1,1;2.0944rad)
  Radius = 6.2
  Refine = true
  SupportTransform = false
  Suppressed = false
  UseAllEdges = false
FEATURE [PartDesign::Body] Body004  label="3DEar"
  AllowCompound = false
  Group = -> [Sketch011,Pad006,Chamfer003,Sketch012,Pad007,Sketch013,Pocket005,Fillet,Fillet001]
  Origin = -> Origin011
  Tip = -> Fillet001
COMPONENT P2 — same part as P1; its construction recipe is shown at P1.
COMPONENT P3 — recipe-attached ("Front cover001", modeled in this document).
Construction recipe (the document's own serialized feature program — sketch geometry with constraints, then the solid features built on it; lengths are millimeters unless a unit is written):

FEATURE [Sketcher::SketchObject] Sketch016  label="CoverPlateSketch"
  ArcFitTolerance = 1e-06
  AttachmentSupport = -> [XZ_Plane018]
  ExternalTypes = [0]
  FullyConstrained = true
  MakeInternals = false
  MapMode = 5
  Placement = pos=(0,0,0) rot=(1,0,0;1.5708rad)
  expr: Constraints[11] = <<Params>>.boxHeight * <<Params>>.rackUnit - <<Params>>.rackUnitTolerance
  expr: Constraints[12] = <<Params>>.boxWidth
  expr: Constraints[15] = <<Params>>.rackUnit * <<Params>>.boxHeight - <<Params>>.rackUnitTolerance - 2 * <<Params>>.frontHoleTopBottomSpace
  expr: Constraints[1] = <<Params>>.M3ScrewHole
  expr: Constraints[20] = (<<Params>>.boxHeight * <<Params>>.rackUnit - <<Params>>.rackUnitTolerance) / 2
  expr: Constraints[21] = <<Params>>.M3InsertDiam / 2 + 5 + <<Params>>.wallThickness
  sketch-geometry (11):
    g0: Circle CenterX=-96.15 CenterY=34.5 CenterZ=0 NormalX=0 NormalY=0 NormalZ=1 AngleXU=0 Radius=1.65
    g1: Circle CenterX=-96.15 CenterY=9.5 CenterZ=0 NormalX=0 NormalY=0 NormalZ=1 AngleXU=0 Radius=1.65
    g2: LineSegment StartX=-105 StartY=44 StartZ=0 EndX=-105 EndY=0 EndZ=0
    g3: LineSegment StartX=-105 StartY=0 StartZ=0 EndX=105 EndY=0 EndZ=0
    g4: LineSegment StartX=105 StartY=0 StartZ=0 EndX=105 EndY=44 EndZ=0
    g5: LineSegment StartX=105 StartY=44 StartZ=0 EndX=-105 EndY=44 EndZ=0
    g6: GeomPoint [constr] X=0 Y=0 Z=0
    g7: LineSegment [constr] StartX=-96.15 StartY=34.5 StartZ=0 EndX=-96.15 EndY=9.5 EndZ=0
    g8: GeomPoint [constr] X=-96.15 Y=22 Z=0
    g9: Circle CenterX=96.15 CenterY=34.5 CenterZ=0 NormalX=0 NormalY=0 NormalZ=1 AngleXU=0 Radius=1.65
    g10: Circle CenterX=96.15 CenterY=9.5 CenterZ=0 NormalX=0 NormalY=0 NormalZ=1 AngleXU=0 Radius=1.65
  constraints (26):
    c: Equal(g0,g1)
    c: Diameter(g0) = 3.3
    c: Coincident(g2,g3)
    c: Coincident(g3,g4)
    c: Coincident(g4,g5)
    c: Coincident(g5,g2)
    c: Vertical(g2)
    c: Vertical(g4)
    c: Horizontal(g3)
    c: Horizontal(g5)
    c: PointOnObject(g3,g-1)
    c: DistanceY(g2,g2) = 44
    c: DistanceX(g3,g3) = 210
    c: Symmetric(g3,g3,g6)
    c: PointOnObject(g6,g-2)
    c: DistanceY(g1,g0) = 25
    c: Coincident(g7,g0)
    c: Coincident(g7,g1)
    c: Vertical(g7)
    c: Symmetric(g7,g7,g8)
    c: DistanceY(g-1,g8) = 22
    c: DistanceX(g2,g1) = 8.85
    c: Equal(g0,g9)
    c: Symmetric(g0,g9,g-2)
    c: Equal(g1,g10)
    c: Symmetric(g1,g10,g-2)
FEATURE [PartDesign::Pad] Pad009  label="CoverPlatePad"
  Direction = (0,-1,2e-16)
  Length = 2
  Length2 = 10
  Placement = pos=(0,0,0) rot=(1,0,0;1.5708rad)
  Profile = -> Sketch016
  ReferenceAxis = -> Sketch016 [N_Axis]
  Refine = true
  SideType = 0
  Suppressed = false
  Type = 0
  Type2 = 0
  expr: Length = <<Params>>.frontThickness
FEATURE [PartDesign::Chamfer] Chamfer004  label="ISO10642"
  Angle = 45
  Base = -> Pad009 [Edge21,Edge24,Edge18,Edge15]
  BaseFeature = -> Pad009
  ChamferType = 0
  FlipDirection = false
  Placement = pos=(0,0,0) rot=(1,0,0;1.5708rad)
  Refine = true
  Size = 1.85
  Size2 = 1
  SupportTransform = false
  Suppressed = false
  UseAllEdges = false
  expr: Size = min(<<Params>>.iso10642coneDetph; <<Params>>.frontThickness - 0.01)
FEATURE [PartDesign::Plane] DatumPlane001  label="VentHoleMidSymmetry"
  AttachmentOffset = pos=(0,0,-22) rot=(0,0,1;0rad)
  AttachmentSupport = -> [Pad009]
  Length = 230.494
  MapMode = 5
  Placement = pos=(0,0,22) rot=(1,0,0;3.14159rad)
  ResizeMode = 0
  Width = 70.4939
  expr: .AttachmentOffset.Base.z = -(<<Params>>.boxHeight * <<Params>>.rackUnit - <<Params>>.rackUnitTolerance) / 2
FEATURE [PartDesign::Mirrored] Mirrored004
  MirrorPlane = -> DatumPlane001
  Placement = pos=(0,0,0) rot=(1,0,0;1.5708rad)
  Refine = true
  Suppressed = false
  TransformMode = 0
FEATURE [Sketcher::SketchObject] Sketch017  label="VentHoleSketch"
  ArcFitTolerance = 1e-06
  AttachmentSupport = -> [Chamfer004]
  ExternalTypes = [0]
  FullyConstrained = true
  MakeInternals = false
  MapMode = 5
  Placement = pos=(0,4.9e-15,0) rot=(-1,0,0;1.5708rad)
  expr: Constraints[18] = <<Params>>.ventHoleDiam
  expr: Constraints[20] = (<<Params>>.rackUnit * <<Params>>.boxHeight - <<Params>>.rackUnitTolerance) / 2
  sketch-geometry (16):
    g0: LineSegment StartX=-3 StartY=-20.2679 StartZ=0 EndX=-3 EndY=-23.7321 EndZ=0
    g1: LineSegment StartX=-3 StartY=-23.7321 StartZ=0 EndX=6.688e-13 EndY=-25.4641 EndZ=0
    g2: LineSegment StartX=6.688e-13 StartY=-25.4641 StartZ=0 EndX=3 EndY=-23.7321 EndZ=0
    g3: LineSegment StartX=3 StartY=-23.7321 StartZ=0 EndX=3 EndY=-20.2679 EndZ=0
    g4: LineSegment StartX=3 StartY=-20.2679 StartZ=0 EndX=-1.8745e-12 EndY=-18.5359 EndZ=0
    g5: LineSegment StartX=-1.8747e-12 StartY=-18.5359 StartZ=0 EndX=-3 EndY=-20.2679 EndZ=0
    g6: Circle [constr] CenterX=-2.914e-13 CenterY=-22 CenterZ=0 NormalX=0 NormalY=0 NormalZ=1 AngleXU=0 Radius=3.4641
    g7: LineSegment StartX=-1 StartY=-16.8038 StartZ=0 EndX=-1 EndY=-13.3397 EndZ=0
    g8: LineSegment StartX=-1 StartY=-13.3397 StartZ=0 EndX=-4 EndY=-11.6077 EndZ=0
    g9: LineSegment StartX=-4 StartY=-11.6077 StartZ=0 EndX=-7 EndY=-13.3397 EndZ=0
    g10: LineSegment StartX=-7 StartY=-13.3397 StartZ=0 EndX=-7 EndY=-16.8038 EndZ=0
    g11: LineSegment StartX=-7 StartY=-16.8038 StartZ=0 EndX=-4 EndY=-18.5359 EndZ=0
    g12: LineSegment StartX=-4 StartY=-18.5359 StartZ=0 EndX=-1 EndY=-16.8038 EndZ=0
    g13: Circle [constr] CenterX=-4 CenterY=-15.0718 CenterZ=0 NormalX=0 NormalY=0 NormalZ=1 AngleXU=0 Radius=3.4641
    g14: LineSegment [constr] StartX=-4 StartY=-18.5359 StartZ=0 EndX=-1.8749e-12 EndY=-18.5359 EndZ=0
    g15: LineSegment [constr] StartX=-1 StartY=-16.8038 StartZ=0 EndX=-1.8747e-12 EndY=-18.5359 EndZ=0
  constraints (38):
    c: Coincident(g0,g1)
    c: Coincident(g1,g2)
    c: Coincident(g2,g3)
    c: Coincident(g3,g4)
    c: Coincident(g4,g5)
    c: Coincident(g5,g0)
    c: Equal(g0, g1-g5) x5
    c: PointOnObject(g0,g6)
    c: PointOnObject(g1,g6)
    c: PointOnObject(g2,g6)
    c: PointOnObject(g3,g6)
    c: PointOnObject(g4,g6)
    c: PointOnObject(g5,g6)
    c: PointOnObject(g6,g-2)
    c: Distance(g2,g0) = 6
    c: Vertical(g0)
    c: DistanceY(g6,g-1) = 22
    c: Coincident(g7,g8)
    c: Coincident(g8,g9)
    c: Coincident(g9,g10)
    c: Coincident(g10,g11)
    c: Coincident(g11,g12)
    c: Coincident(g12,g7)
    c: Equal(g7, g8-g12) x5
    c: PointOnObject(g7,g13)
    c: PointOnObject(g8,g13)
    c: PointOnObject(g9,g13)
    c: PointOnObject(g10,g13)
    c: PointOnObject(g11,g13)
    c: PointOnObject(g12,g13)
    c: Equal(g7,g3)
    c: Parallel(g7,g3)
    c: Coincident(g14,g11)
    c: Coincident(g14,g4)
    c: Horizontal(g14)
    c: Coincident(g15,g7)
    c: Coincident(g15,g4)
    c: Perpendicular(g12,g15)
FEATURE [PartDesign::LinearPattern] LinearPattern005
  Direction = -> Sketch017 [H_Axis]
  Length = 80
  Length2 = 100
  Mode = 1
  Mode2 = 0
  Occurrences = 11
  Occurrences2 = 1
  Offset = 8
  Offset2 = 10
  Placement = pos=(0,0,0) rot=(1,0,0;1.5708rad)
  Refine = true
  Reversed2 = false
  SpacingPattern = [0]
  SpacingPattern2 = [0]
  Spacings = [-1,-1,-1,-1,-1,-1,-1,-1,-1,-1]
  Suppressed = false
  TransformMode = 0
  expr: Occurrences = (<<Params>>.boxWidth / 2 - <<Params>>.wallThickness - 15) / (<<Params>>.ventHoleDiam * 4 / 3)
  expr: Offset = <<Params>>.ventHoleDiam * 4 / 3
FEATURE [PartDesign::LinearPattern] LinearPattern006
  Direction = -> Sketch017 [V_Axis]
  Length = 14
  Length2 = 100
  Mode = 1
  Mode2 = 0
  Occurrences = 2
  Occurrences2 = 1
  Offset = 14
  Offset2 = 10
  Placement = pos=(0,0,0) rot=(1,0,0;1.5708rad)
  Refine = true
  Reversed2 = false
  SpacingPattern = [0]
  SpacingPattern2 = [0]
  Spacings = [-1]
  Suppressed = false
  TransformMode = 0
  expr: Occurrences = max(round(<<Params>>.rackUnit * <<Params>>.boxHeight - 2 * <<Params>>.wallThickness) / (<<Params>>.ventHoleDiam * 4 * cos(30)) - 1; 2)
  expr: Offset = <<Params>>.ventHoleDiam * (2 * 3 + 1) / 3
FEATURE [PartDesign::Mirrored] Mirrored003
  MirrorPlane = -> Sketch017 [V_Axis]
  Placement = pos=(0,0,0) rot=(1,0,0;1.5708rad)
  Refine = true
  Suppressed = false
  TransformMode = 0
FEATURE [Sketcher::SketchObject] Sketch019  label="KeystoneHolderSlab"
  ArcFitTolerance = 1e-06
  AttachmentSupport = -> [Chamfer004]
  ExternalTypes = [0]
  FullyConstrained = true
  MakeInternals = false
  MapMode = 5
  Placement = pos=(0,-2,0) rot=(1,0,0;1.5708rad)
  expr: Constraints[10] = <<Params>>.wallThickness + 2
  expr: Constraints[11] = min(4.2 + (4.2 + <<Params>>.keystoneHoleWidth) * <<Params>>.keystoneFrontX; <<Params>>.boxWidth - 2 * (<<Params>>.wallThickness * 2 + 10 + <<Params>>.M3InsertDiam))
  expr: Constraints[12] = min(<<Params>>.boxHeight * <<Params>>.rackUnit - <<Params>>.rackUnitTolerance - 4 * <<Params>>.wallThickness; 3 + min(<<Params>>.keystoneFrontY; <<Params>>.boxHeight) * (<<Params>>.keystoneCatchHeight + 3) + (<<Params>>.keystoneFrontY - 1) * 1)
  sketch-geometry (5):
    g0: LineSegment StartX=-49.6 StartY=29.55 StartZ=0 EndX=-49.6 EndY=3.75 EndZ=0
    g1: LineSegment StartX=-49.6 StartY=3.75 StartZ=0 EndX=49.6 EndY=3.75 EndZ=0
    g2: LineSegment StartX=49.6 StartY=3.75 StartZ=0 EndX=49.6 EndY=29.55 EndZ=0
    g3: LineSegment StartX=49.6 StartY=29.55 StartZ=0 EndX=-49.6 EndY=29.55 EndZ=0
    g4: GeomPoint X=0 Y=3.75 Z=0
  constraints (13):
    c: Coincident(g0,g1)
    c: Coincident(g1,g2)
    c: Coincident(g2,g3)
    c: Coincident(g3,g0)
    c: Vertical(g0)
    c: Vertical(g2)
    c: Horizontal(g1)
    c: Horizontal(g3)
    c: Symmetric(g1,g1,g4)
    c: PointOnObject(g4,g-2)
    c: DistanceY(g-1,g4) = 3.75
    c: Distance(g3,g3) = 99.2
    c: DistanceY(g2,g2) = 25.8
FEATURE [PartDesign::LinearPattern] LinearPattern013
  Direction = -> X_Axis019
  Length = 76
  Length2 = 100
  Mode = 1
  Mode2 = 0
  Occurrences = 5
  Occurrences2 = 1
  Offset = 19
  Offset2 = 10
  Placement = pos=(0,0,0) rot=(1,0,0;1.5708rad)
  Refine = true
  Reversed2 = false
  SpacingPattern = [0]
  SpacingPattern2 = [0]
  Spacings = [-1,-1,-1,-1]
  Suppressed = false
  TransformMode = 0
  expr: Occurrences = <<Params>>.keystoneFrontX
  expr: Offset = <<Params>>.keystoneHoleWidth + 4.2
FEATURE [PartDesign::LinearPattern] LinearPattern014
  Direction = -> Z_Axis019
  Length = 25.8
  Length2 = 100
  Mode = 1
  Mode2 = 0
  Occurrences = 1
  Occurrences2 = 1
  Offset = 25.8
  Offset2 = 10
  Placement = pos=(0,0,0) rot=(1,0,0;1.5708rad)
  Refine = true
  Reversed2 = false
  SpacingPattern = [0]
  SpacingPattern2 = [0]
  Spacings2 = [0]
  Suppressed = false
  TransformMode = 0
  expr: Occurrences = <<Params>>.keystoneFrontY
  expr: Offset = <<Params>>.keystoneCatchHeight + 3 + 3
FEATURE [Sketcher::SketchObject] Sketch037
  ArcFitTolerance = 1e-06
  AttachmentSupport = -> [Chamfer004]
  ExternalTypes = [0]
  FullyConstrained = true
  MakeInternals = false
  MapMode = 5
  Placement = pos=(0,-2,0) rot=(1,0,0;1.5708rad)
  expr: Constraints[11] = <<Params>>.boxWidth - 2 * (<<Params>>.fitTol + <<Params>>.wallThickness + 5 + <<Params>>.M3InsertDiam + 5)
  expr: Constraints[13] = (<<Params>>.rackUnit * <<Params>>.boxHeight - <<Params>>.rackUnitTolerance) / 2
  expr: Constraints[8] = <<Params>>.rackUnit * <<Params>>.boxHeight - <<Params>>.rackUnitTolerance - 2 * <<Params>>.wallThickness - 2 * <<Params>>.fitTol
  sketch-geometry (6):
    g0: LineSegment StartX=-88.8 StartY=42 StartZ=0 EndX=-88.8 EndY=2 EndZ=0
    g1: LineSegment StartX=-88.8 StartY=2 StartZ=0 EndX=88.8 EndY=2 EndZ=0
    g2: LineSegment StartX=88.8 StartY=2 StartZ=0 EndX=88.8 EndY=42 EndZ=0
    g3: LineSegment StartX=88.8 StartY=42 StartZ=0 EndX=-88.8 EndY=42 EndZ=0
    g4: GeomPoint X=0 Y=2 Z=0
    g5: GeomPoint X=88.8 Y=22 Z=0
  constraints (14):
    c: Coincident(g0,g1)
    c: Coincident(g1,g2)
    c: Coincident(g2,g3)
    c: Coincident(g3,g0)
    c: Vertical(g0)
    c: Vertical(g2)
    c: Horizontal(g1)
    c: Horizontal(g3)
    c: DistanceY(g2,g2) = 40
    c: Symmetric(g1,g1,g4)
    c: PointOnObject(g4,g-2)
    c: DistanceX(g3,g3) = 177.6
    c: Symmetric(g2,g2,g5)
    c: DistanceY(g-1,g5) = 22
FEATURE [PartDesign::Pad] Pad015
  BaseFeature = -> Chamfer004
  Direction = (0,-1,2e-16)
  Length = 3.75
  Length2 = 10
  Placement = pos=(0,0,0) rot=(1,0,0;1.5708rad)
  Profile = -> Sketch037
  ReferenceAxis = -> Sketch037 [N_Axis]
  Refine = true
  Reversed = true
  SideType = 0
  Suppressed = false
  Type = 0
  Type2 = 0
  expr: Length = <<Params>>.frontThickness + <<Params>>.wallThickness
FEATURE [PartDesign::Pocket] Pocket007  label="VentHolePocket"
  BaseFeature = -> Pad015
  Direction = (0,-1,-2e-16)
  Length = 2
  Length2 = 1.75
  Placement = pos=(0,0,0) rot=(1,0,0;1.5708rad)
  Profile = -> Sketch017
  ReferenceAxis = -> Sketch017 [N_Axis]
  Refine = true
  SideType = 1
  Suppressed = false
  Type = 0
  Type2 = 0
  expr: Length = <<Params>>.frontThickness
  expr: Length2 = <<Params>>.wallThickness
FEATURE [PartDesign::MultiTransform] MultiTransform002  label="VentHolesTransform"
  BaseFeature = -> Pocket007
  Originals = -> [Pocket007]
  Placement = pos=(0,0,0) rot=(1,0,0;1.5708rad)
  Refine = true
  Suppressed = false
  TransformMode = 0
  Transformations = -> [LinearPattern005,LinearPattern006,Mirrored003,Mirrored004]
FEATURE [Sketcher::SketchObject] Sketch018  label="MinContour"
  ArcFitTolerance = 1e-06
  AttachmentSupport = -> [Pad015]
  ExternalTypes = [0]
  FullyConstrained = true
  MakeInternals = false
  MapMode = 5
  Placement = pos=(0,-2,9e-16) rot=(1,0,0;1.5708rad)
  expr: Constraints[22] = <<Params>>.boxHeight * <<Params>>.rackUnit - <<Params>>.rackUnitTolerance - 2 * <<Params>>.wallThickness
  expr: Constraints[25] = <<Params>>.boxWidth - 2 * (5 + 5 + <<Params>>.M3InsertDiam + <<Params>>.wallThickness)
  expr: Constraints[8] = <<Params>>.wallThickness
  sketch-geometry (11):
    g0: LineSegment StartX=-89.05 StartY=42.25 StartZ=0 EndX=89.05 EndY=42.25 EndZ=0
    g1: LineSegment StartX=89.05 StartY=42.25 StartZ=0 EndX=89.05 EndY=44 EndZ=0
    g2: LineSegment StartX=89.05 StartY=44 StartZ=0 EndX=-89.05 EndY=44 EndZ=0
    g3: LineSegment StartX=-89.05 StartY=44 StartZ=0 EndX=-89.05 EndY=42.25 EndZ=0
    g4: LineSegment [constr] StartX=-89.05 StartY=42.25 StartZ=0 EndX=-89.05 EndY=0 EndZ=0
    g5: LineSegment [constr] StartX=89.05 StartY=42.25 StartZ=0 EndX=89.05 EndY=1.75 EndZ=0
    g6: LineSegment StartX=-89.05 StartY=0 StartZ=0 EndX=89.05 EndY=0 EndZ=0
    g7: LineSegment StartX=89.05 StartY=0 StartZ=0 EndX=89.05 EndY=1.75 EndZ=0
    g8: LineSegment StartX=89.05 StartY=1.75 StartZ=0 EndX=-89.05 EndY=1.75 EndZ=0
    g9: LineSegment StartX=-89.05 StartY=1.75 StartZ=0 EndX=-89.05 EndY=0 EndZ=0
    g10: GeomPoint X=0 Y=0 Z=0
  constraints (29):
    c: Coincident(g0,g1)
    c: Coincident(g1,g2)
    c: Coincident(g2,g3)
    c: Coincident(g3,g0)
    c: Horizontal(g0)
    c: Horizontal(g2)
    c: Vertical(g1)
    c: Vertical(g3)
    c: DistanceY(g1,g1) = 1.75
    c: Coincident(g4,g0)
    c: Vertical(g4)
    c: Coincident(g5,g0)
    c: Vertical(g5)
    c: Coincident(g6,g7)
    c: Coincident(g7,g8)
    c: Coincident(g8,g9)
    c: Coincident(g9,g6)
    c: Horizontal(g6)
    c: Horizontal(g8)
    c: Vertical(g7)
    c: Vertical(g9)
    c: Coincident(g6,g4)
    c: DistanceY(g7,g0) = 40.5
    c: Equal(g9,g3)
    c: PointOnObject(g-1,g6)
    c: DistanceX(g2,g2) = 178.1
    c: Coincident(g5,g7)
    c: Symmetric(g6,g6,g10)
    c: PointOnObject(g10,g-2)
FEATURE [PartDesign::Pad] Pad010  label="MinContourPad"
  BaseFeature = -> MultiTransform002
  Direction = (0,-1,2e-16)
  Length = 10
  Length2 = 10
  Placement = pos=(0,0,0) rot=(1,0,0;1.5708rad)
  Profile = -> Sketch018
  ReferenceAxis = -> Sketch018 [N_Axis]
  Refine = true
  SideType = 0
  Suppressed = false
  Type = 3
  Type2 = 0
  UpToFace = -> Pad015 [Face3]
FEATURE [PartDesign::Pad] Pad011  label="KeystoneHolderSlabPad"
  BaseFeature = -> Pad010
  Direction = (0,-1,2e-16)
  Length = 9.75
  Length2 = 10
  Placement = pos=(0,0,0) rot=(1,0,0;1.5708rad)
  Profile = -> Sketch019
  ReferenceAxis = -> Sketch019 [N_Axis]
  Refine = true
  Reversed = true
  SideType = 0
  Suppressed = false
  Type = 0
  Type2 = 0
  expr: Length = <<Params>>.keystoneStopDepth
FEATURE [Sketcher::SketchObject] Sketch020  label="KeystoneHole"
  ArcFitTolerance = 1e-06
  AttachmentSupport = -> [Pad011]
  ExternalTypes = [0]
  FullyConstrained = true
  MakeInternals = false
  MapMode = 5
  Placement = pos=(0,7.75,-1.7e-15) rot=(-1,0,0;1.5708rad)
  expr: Constraints[10] = <<Params>>.wallThickness + 2 + 3
  expr: Constraints[11] = min(4.2 + (4.2 + <<Params>>.keystoneHoleWidth) * <<Params>>.keystoneFrontX; <<Params>>.boxWidth - 2 * (<<Params>>.wallThickness * 2 + 10 + <<Params>>.M3InsertDiam)) / 2 - 4.2
  expr: Constraints[8] = <<Params>>.keystoneHoleWidth
  expr: Constraints[9] = <<Params>>.keystoneHoleHeight
  sketch-geometry (4):
    g0: LineSegment StartX=-45.4 StartY=-6.75 StartZ=0 EndX=-45.4 EndY=-23.55 EndZ=0
    g1: LineSegment StartX=-45.4 StartY=-23.55 StartZ=0 EndX=-30.6 EndY=-23.55 EndZ=0
    g2: LineSegment StartX=-30.6 StartY=-23.55 StartZ=0 EndX=-30.6 EndY=-6.75 EndZ=0
    g3: LineSegment StartX=-30.6 StartY=-6.75 StartZ=0 EndX=-45.4 EndY=-6.75 EndZ=0
  constraints (12):
    c: Coincident(g0,g1)
    c: Coincident(g1,g2)
    c: Coincident(g2,g3)
    c: Coincident(g3,g0)
    c: Vertical(g0)
    c: Vertical(g2)
    c: Horizontal(g1)
    c: Horizontal(g3)
    c: DistanceX(g3,g3) = 14.8
    c: DistanceY(g2,g2) = 16.8
    c: DistanceY(g0,g-1) = 6.75
    c: DistanceX(g0,g-1) = 45.4
FEATURE [PartDesign::Pocket] Pocket008  label="KeystoneHolePocket"
  BaseFeature = -> Pad011
  Direction = (0,-1,-2e-16)
  Length = 5
  Length2 = 5
  Placement = pos=(0,0,0) rot=(1,0,0;1.5708rad)
  Profile = -> Sketch020
  ReferenceAxis = -> Sketch020 [N_Axis]
  Refine = true
  SideType = 0
  Suppressed = false
  Type = 1
  Type2 = 0
FEATURE [Sketcher::SketchObject] Sketch021  label="KeystoneCatchDepth"
  ArcFitTolerance = 1e-06
  AttachmentSupport = -> [Pocket008]
  ExternalTypes = [0]
  FullyConstrained = true
  MakeInternals = false
  MapMode = 5
  Placement = pos=(0,7.75,-1.7e-15) rot=(-1,0,0;1.5708rad)
  expr: Constraints[10] = <<Params>>.wallThickness * 2 + <<Params>>.fitTol + 3
  expr: Constraints[11] = min(4.2 + (4.2 + <<Params>>.keystoneHoleWidth) * <<Params>>.keystoneFrontX; <<Params>>.boxWidth - 2 * (<<Params>>.wallThickness * 2 + 10 + <<Params>>.M3InsertDiam)) / 2 - 4.2
  expr: Constraints[8] = <<Params>>.keystoneHoleWidth
  expr: Constraints[9] = <<Params>>.keystoneCatchHeight
  sketch-geometry (4):
    g0: LineSegment StartX=-45.4 StartY=-26.55 StartZ=0 EndX=-30.6 EndY=-26.55 EndZ=0
    g1: LineSegment StartX=-30.6 StartY=-26.55 StartZ=0 EndX=-30.6 EndY=-6.75 EndZ=0
    g2: LineSegment StartX=-30.6 StartY=-6.75 StartZ=0 EndX=-45.4 EndY=-6.75 EndZ=0
    g3: LineSegment StartX=-45.4 StartY=-6.75 StartZ=0 EndX=-45.4 EndY=-26.55 EndZ=0
  constraints (12):
    c: Coincident(g0,g1)
    c: Coincident(g1,g2)
    c: Coincident(g2,g3)
    c: Coincident(g3,g0)
    c: Horizontal(g0)
    c: Horizontal(g2)
    c: Vertical(g1)
    c: Vertical(g3)
    c: Distance(g2,g2) = 14.8
    c: DistanceY(g1,g1) = 19.8
    c: DistanceY(g1,g-1) = 6.75
    c: DistanceX(g2,g-1) = 45.4
FEATURE [PartDesign::Pocket] Pocket009  label="KeystoneCatchDepthPocket"
  BaseFeature = -> Pocket008
  Direction = (0,-1,-2e-16)
  Length = 8.2
  Length2 = 5
  Placement = pos=(0,0,0) rot=(1,0,0;1.5708rad)
  Profile = -> Sketch021
  ReferenceAxis = -> Sketch021 [N_Axis]
  Refine = true
  SideType = 0
  Suppressed = false
  Type = 0
  Type2 = 0
  expr: Length = <<Params>>.keystoneCatchDepth
FEATURE [Sketcher::SketchObject] Sketch022  label="CatchHoles"
  ArcFitTolerance = 1e-06
  AttachmentSupport = -> [Pocket009]
  ExternalTypes = [0]
  FullyConstrained = true
  MakeInternals = false
  MapMode = 5
  Placement = pos=(-49.6,0,0) rot=(0.707107,0,-0.707107;3.14159rad)
  expr: Constraints[19] = <<Params>>.keystoneCatchHeight
  expr: Constraints[23] = <<Params>>.keystoneCatchDepth - <<Params>>.frontThickness
  sketch-geometry (8):
    g0: LineSegment StartX=-28.05 StartY=-6.2 StartZ=0 EndX=-26.55 EndY=-6.2 EndZ=0
    g1: LineSegment StartX=-26.55 StartY=-6.2 StartZ=0 EndX=-26.55 EndY=-3.2 EndZ=0
    g2: LineSegment StartX=-26.55 StartY=-3.2 StartZ=0 EndX=-28.05 EndY=-3.2 EndZ=0
    g3: LineSegment StartX=-28.05 StartY=-3.2 StartZ=0 EndX=-28.05 EndY=-6.2 EndZ=0
    g4: LineSegment StartX=-6.75 StartY=-3.2 StartZ=0 EndX=-6.75 EndY=-6.2 EndZ=0
    g5: LineSegment StartX=-6.75 StartY=-6.2 StartZ=0 EndX=-5.25 EndY=-6.2 EndZ=0
    g6: LineSegment StartX=-5.25 StartY=-6.2 StartZ=0 EndX=-5.25 EndY=-3.2 EndZ=0
    g7: LineSegment StartX=-5.25 StartY=-3.2 StartZ=0 EndX=-6.75 EndY=-3.2 EndZ=0
  constraints (24):
    c: Coincident(g0,g1)
    c: Coincident(g1,g2)
    c: Coincident(g2,g3)
    c: Coincident(g3,g0)
    c: Horizontal(g0)
    c: Horizontal(g2)
    c: Vertical(g1)
    c: Vertical(g3)
    c: Coincident(g4,g5)
    c: Coincident(g5,g6)
    c: Coincident(g6,g7)
    c: Coincident(g7,g4)
    c: Vertical(g4)
    c: Vertical(g6)
    c: Horizontal(g5)
    c: Horizontal(g7)
    c: Equal(g7,g0)
    c: Equal(g4,g3)
    c: DistanceX(g5,g5) = 1.5
    c: DistanceX(g1,g4) = 19.8
    c: DistanceX(g4,g-1) = 6.75
    c: PointOnObject(g4,g2)
    c: DistanceY(g4,g4) = 3
    c: DistanceY(g5,g-1) = 6.2
FEATURE [PartDesign::Pocket] Pocket010  label="CatchHolesPocket"
  BaseFeature = -> Pocket009
  Direction = (1,0,2e-16)
  Length = 19
  Length2 = -4.2
  Placement = pos=(0,0,0) rot=(1,0,0;1.5708rad)
  Profile = -> Sketch022
  ReferenceAxis = -> Sketch022 [N_Axis]
  Refine = true
  SideType = 1
  Suppressed = false
  Type = 0
  Type2 = 0
  expr: Length = <<Params>>.keystoneHoleWidth + 4.2
  expr: Length2 = -4.2
FEATURE [PartDesign::Chamfer] Chamfer005  label="KeystoneInsertChamfer"
  Angle = 45
  Base = -> Pocket010 [Edge2134,Edge1712,Edge2132]
  BaseFeature = -> Pocket010
  ChamferType = 0
  FlipDirection = false
  Placement = pos=(0,0,0) rot=(1,0,0;1.5708rad)
  Refine = true
  Size = 1
  Size2 = 1
  SupportTransform = false
  Suppressed = false
  UseAllEdges = false
FEATURE [PartDesign::MultiTransform] MultiTransform006
  BaseFeature = -> Chamfer005
  Originals = -> [Pocket010,Chamfer005,Pocket009,Pocket008]
  Placement = pos=(0,0,0) rot=(1,0,0;1.5708rad)
  Refine = true
  Suppressed = false
  TransformMode = 0
  Transformations = -> [LinearPattern013,LinearPattern014]
FEATURE [PartDesign::Body] Body005  label="frontCoverVented001"
  AllowCompound = false
  Group = -> [Sketch016,Pad009,Chamfer004,Sketch017,Sketch037,Pad015,Pocket007,LinearPattern005,LinearPattern006,Sketch018,Mirrored003,DatumPlane001,Mirrored004,MultiTransform002,Pad010,Sketch019,Pad011,Sketch020,Pocket008,Sketch021,Pocket009,Sketch022,Pocket010,Chamfer005,MultiTransform006,LinearPattern013,LinearPattern014]
  Origin = -> Origin019
  Tip = -> MultiTransform006
COMPONENT P4 — geometry summary ("NF-A4x10 FLX001"; no construction recipe available for this part):
  bounding box: 40.0 x 40.0 x 12.1 mm
  tessellated surface: 178,094 triangles
  volume: 5674 mm^3 (29% of its bounding box)
COMPONENT P5 — recipe-attached ("Top Cover001", modeled in this document).
Construction recipe (the document's own serialized feature program — sketch geometry with constraints, then the solid features built on it; lengths are millimeters unless a unit is written):

FEATURE [Sketcher::SketchObject] Sketch031
  ArcFitTolerance = 1e-06
  AttachmentSupport = -> [XY_Plane024]
  ExternalTypes = [0]
  FullyConstrained = true
  MakeInternals = false
  MapMode = 5
  expr: Constraints[37] = 5 + <<Params>>.M3InsertDiam / 2 - <<Params>>.fitTol / 2
  expr: Constraints[38] = 17.6 - <<Params>>.fitTol / 2
  expr: Constraints[39] = 5 + <<Params>>.M3InsertDiam / 2
  expr: Constraints[6] = <<Params>>.boxWidth - <<Params>>.wallThickness * 2 - <<Params>>.fitTol
  expr: Constraints[7] = <<Params>>.boxLength - <<Params>>.wallThickness - <<Params>>.fitTol
  expr: Constraints[9] = <<Params>>.M3ScrewHole
  sketch-geometry (18):
    g0: LineSegment StartX=-103.125 StartY=88 StartZ=0 EndX=-103.125 EndY=-88 EndZ=0
    g1: LineSegment StartX=-102.125 StartY=-89 StartZ=0 EndX=102.125 EndY=-89 EndZ=0
    g2: LineSegment StartX=103.125 StartY=-88 StartZ=0 EndX=103.125 EndY=88 EndZ=0
    g3: LineSegment StartX=102.125 StartY=89 StartZ=0 EndX=-102.125 EndY=89 EndZ=0
    g4: GeomPoint [constr] X=0 Y=0 Z=0
    g5: Circle CenterX=-96.025 CenterY=82.025 CenterZ=0 NormalX=0 NormalY=0 NormalZ=1 AngleXU=0 Radius=1.65
    g6: Circle CenterX=-96.025 CenterY=-71.525 CenterZ=0 NormalX=0 NormalY=0 NormalZ=1 AngleXU=0 Radius=1.65
    g7: Circle CenterX=96.025 CenterY=82.025 CenterZ=0 NormalX=0 NormalY=0 NormalZ=1 AngleXU=0 Radius=1.65
    g8: Circle CenterX=96.025 CenterY=-71.525 CenterZ=0 NormalX=0 NormalY=0 NormalZ=1 AngleXU=0 Radius=1.65
    g9: ArcOfCircle CenterX=-102.125 CenterY=88 CenterZ=0 NormalX=0 NormalY=0 NormalZ=1 AngleXU=0 Radius=1 StartAngle=1.5708 EndAngle=3.14159
    g10: GeomPoint [constr] X=-103.125 Y=89 Z=0
    g11: ArcOfCircle CenterX=-102.125 CenterY=-88 CenterZ=0 NormalX=0 NormalY=0 NormalZ=1 AngleXU=0 Radius=1 StartAngle=3.14159 EndAngle=4.71239
    g12: GeomPoint [constr] X=-103.125 Y=-89 Z=0
    g13: ArcOfCircle CenterX=102.125 CenterY=-88 CenterZ=0 NormalX=0 NormalY=0 NormalZ=1 AngleXU=0 Radius=1 StartAngle=4.71239 EndAngle=6.28319
    g14: GeomPoint [constr] X=103.125 Y=-89 Z=0
    g15: ArcOfCircle CenterX=102.125 CenterY=88 CenterZ=0 NormalX=0 NormalY=0 NormalZ=1 AngleXU=0 Radius=1 StartAngle=1.7e-15 EndAngle=1.5708
    g16: GeomPoint [constr] X=103.125 Y=89 Z=0
    g17: LineSegment [constr] StartX=-96.025 StartY=-71.525 StartZ=0 EndX=-96.025 EndY=82.025 EndZ=0
  constraints (40):
    c: Vertical(g0)
    c: Vertical(g2)
    c: Horizontal(g1)
    c: Horizontal(g3)
    c: Symmetric(g14,g10,g4)
    c: Coincident(g4,g-1)
    c: DistanceX(g10,g16) = 206.25
    c: DistanceY(g14,g16) = 178
    c: Equal(g6,g5)
    c: Diameter(g5) = 3.3
    c: Equal(g5,g7)
    c: Symmetric(g5,g7,g-2)
    c: Equal(g6,g8)
    c: Symmetric(g6,g8,g-2)
    c: PointOnObject(g10,g3)
    c: PointOnObject(g10,g0)
    c: Tangent(g3,g9) = -1.5708
    c: Tangent(g0,g9) = -1.5708
    c: PointOnObject(g12,g0)
    c: PointOnObject(g12,g1)
    c: Tangent(g0,g11) = -1.5708
    c: Tangent(g1,g11) = -1.5708
    c: PointOnObject(g14,g1)
    c: PointOnObject(g14,g2)
    c: Tangent(g1,g13) = -1.5708
    c: Tangent(g2,g13) = -1.5708
    c: PointOnObject(g16,g2)
    c: PointOnObject(g16,g3)
    c: Tangent(g2,g15) = -1.5708
    c: Tangent(g3,g15) = -1.5708
    c: Equal(g15,g9)
    c: Equal(g9,g11)
    c: Equal(g11,g13)
    c: Radius(g9) = 1
    c: Coincident(g17,g6)
    c: Coincident(g17,g5)
    c: Vertical(g17)
    c: Distance(g5,g3) = 6.975
    c: DistanceY(g12,g6) = 17.475
    c: Distance(g0,g17) = 7.1
FEATURE [PartDesign::Pad] Pad013
  Direction = (0,0,1)
  Length = 1.75
  Length2 = 10
  Profile = -> Sketch031
  ReferenceAxis = -> Sketch031 [N_Axis]
  Refine = true
  SideType = 0
  Suppressed = false
  Type = 0
  Type2 = 0
  expr: Length = <<Params>>.wallThickness
FEATURE [PartDesign::Chamfer] Chamfer
  Angle = 45
  Base = -> Pad013 [Edge27,Edge33,Edge30,Edge36]
  BaseFeature = -> Pad013
  ChamferType = 0
  FlipDirection = false
  Refine = true
  Size = 1.74
  Size2 = 1
  SupportTransform = false
  Suppressed = false
  UseAllEdges = false
  expr: Size = min(<<Params>>.wallThickness - 0.01; <<Params>>.iso10642coneDetph)
FEATURE [PartDesign::Body] Body006  label="topCover"
  AllowCompound = false
  Group = -> [Sketch031,Pad013,Chamfer]
  Origin = -> Origin024
  Tip = -> Chamfer
PROVENANCE & LICENSES
A FreeCAD (.FCStd) document from a public repository crawl; recipes are the document's own serialized feature recipes (and, for linked parts, companion documents' recipes).
License: cc-by-sa-4.0.
